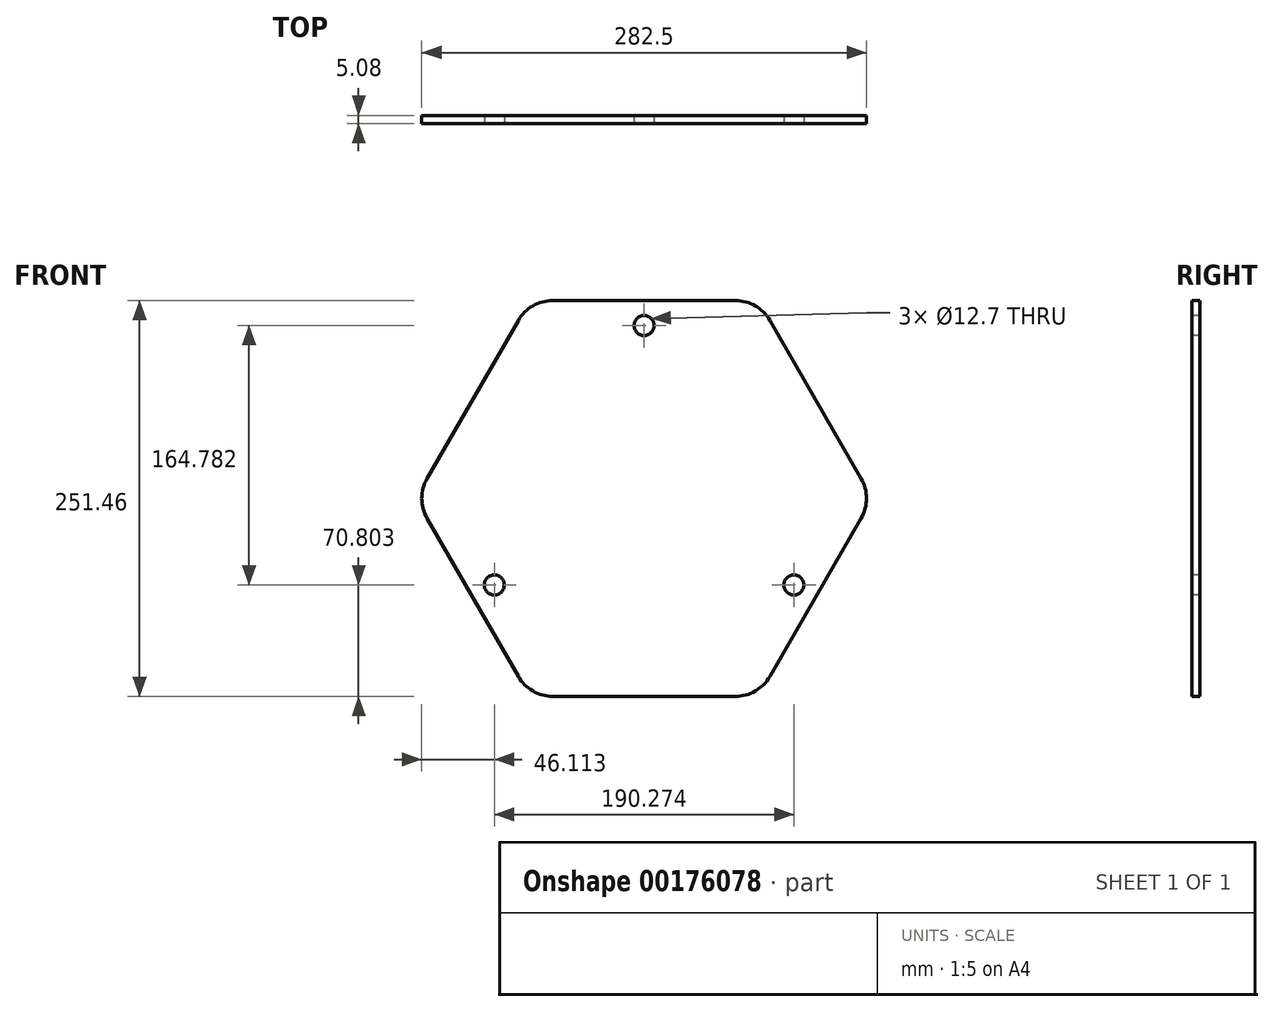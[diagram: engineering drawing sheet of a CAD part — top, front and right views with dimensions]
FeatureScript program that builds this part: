
annotation { "Feature Type Name" : "Feature", "Feature Type Description" : "" }
export const myFeature = defineFeature(function(context is Context, id is Id, definition is map)
    precondition{}
    {
        {
            var Q0;
            Q0=qCreatedBy(makeId("Front.planeOp"),FACE);
            var sketch = newSketch(context, id + "F0", { "sketchPlane" : qUnion([Q0])});
            skCircle(sketch, "E0.cCircle", {"center": v(0, 0) * mm, "radius": 125.73 * mm, "construction": true});
            skLineSegment(sketch, "E0.0", {"start": v(79.92, 113.03) * mm, "end": v(137.85, 12.7) * mm});
            skLineSegment(sketch, "E0.1", {"start": v(137.85, -12.7) * mm, "end": v(79.92, -113.03) * mm});
            skLineSegment(sketch, "E0.2", {"start": v(57.93, -125.73) * mm, "end": v(-57.93, -125.73) * mm});
            skLineSegment(sketch, "E0.3", {"start": v(-79.92, -113.03) * mm, "end": v(-137.85, -12.7) * mm});
            skLineSegment(sketch, "E0.4", {"start": v(-137.85, 12.7) * mm, "end": v(-79.92, 113.03) * mm});
            skLineSegment(sketch, "E0.5", {"start": v(-57.93, 125.73) * mm, "end": v(57.93, 125.73) * mm});
            skPoint(sketch, "E0.0.midPoint", {"position": v(108.89, 62.86) * mm});
            skPoint(sketch, "E1.0.midPoint", {"position": v(0, 93.98) * mm});
            skPoint(sketch, "E2.visualSharp", {"position": v(-72.6, 125.73) * mm});
            skArc(sketch, "E2.filletArc", {"start": v(-57.93, 125.73) * mm, "mid": v(-70.63, 122.33) * mm, "end": v(-79.92, 113.03) * mm});
            skPoint(sketch, "E3.visualSharp", {"position": v(72.6, 125.73) * mm});
            skArc(sketch, "E3.filletArc", {"start": v(79.92, 113.03) * mm, "mid": v(70.63, 122.33) * mm, "end": v(57.93, 125.73) * mm});
            skPoint(sketch, "E4.visualSharp", {"position": v(-145.18, 0) * mm});
            skArc(sketch, "E4.filletArc", {"start": v(-137.85, 12.7) * mm, "mid": v(-141.25, 0) * mm, "end": v(-137.85, -12.7) * mm});
            skPoint(sketch, "E5.visualSharp", {"position": v(145.18, 0) * mm});
            skArc(sketch, "E5.filletArc", {"start": v(137.85, -12.7) * mm, "mid": v(141.25, 0) * mm, "end": v(137.85, 12.7) * mm});
            skPoint(sketch, "E6.visualSharp", {"position": v(-72.6, -125.73) * mm});
            skArc(sketch, "E6.filletArc", {"start": v(-79.92, -113.03) * mm, "mid": v(-70.63, -122.33) * mm, "end": v(-57.93, -125.73) * mm});
            skPoint(sketch, "E7.visualSharp", {"position": v(72.6, -125.73) * mm});
            skArc(sketch, "E7.filletArc", {"start": v(57.93, -125.73) * mm, "mid": v(70.63, -122.33) * mm, "end": v(79.92, -113.03) * mm});
            skPoint(sketch, "E8.visualSharp", {"position": v(-54.26, 93.98) * mm});
            skPoint(sketch, "E9.visualSharp", {"position": v(54.26, 93.98) * mm});
            skPoint(sketch, "E10.visualSharp", {"position": v(108.52, 0) * mm});
            skPoint(sketch, "E11.visualSharp", {"position": v(54.26, -93.98) * mm});
            skPoint(sketch, "E12.visualSharp", {"position": v(-54.26, -93.98) * mm});
            skPoint(sketch, "E13.visualSharp", {"position": v(-108.52, 0) * mm});
            skSolve(sketch);
        }
        {
            var Q0;
            Q0=makeQuery(id+"F0.imprint","IMPRINT",FACE,{"disambiguationData":[TD([[makeQuery(id+"F0.imprint","IMPRINT",EDGE,{"derivedFrom":sQuery(id+"F0.wireOp",EDGE,"E0.0")}),-1.0]])]});
            extrude(context, id + "F1", {"entities" : qUnion([Q0]), "depth" : 5.08 * mm});
        }
        {
            var Q0;
            Q0=makeQuery(id+"F1.opExtrude","CAP_FACE",FACE,{"disambiguationData":[OSD([sQuery(id+"F0.wireOp",EDGE,"E0.0"),sQuery(id+"F0.wireOp",EDGE,"E0.1"),sQuery(id+"F0.wireOp",EDGE,"E0.2"),sQuery(id+"F0.wireOp",EDGE,"E0.3"),sQuery(id+"F0.wireOp",EDGE,"E0.4"),sQuery(id+"F0.wireOp",EDGE,"E0.5"),sQuery(id+"F0.wireOp",EDGE,"E1.0"),sQuery(id+"F0.wireOp",EDGE,"E1.1"),sQuery(id+"F0.wireOp",EDGE,"E1.2"),sQuery(id+"F0.wireOp",EDGE,"E1.3"),sQuery(id+"F0.wireOp",EDGE,"E1.4"),sQuery(id+"F0.wireOp",EDGE,"E1.5"),sQuery(id+"F0.wireOp",EDGE,"E2.filletArc"),sQuery(id+"F0.wireOp",EDGE,"E3.filletArc"),sQuery(id+"F0.wireOp",EDGE,"E4.filletArc"),sQuery(id+"F0.wireOp",EDGE,"E5.filletArc"),sQuery(id+"F0.wireOp",EDGE,"E6.filletArc"),sQuery(id+"F0.wireOp",EDGE,"E7.filletArc"),sQuery(id+"F0.wireOp",EDGE,"E8.filletArc"),sQuery(id+"F0.wireOp",EDGE,"E9.filletArc"),sQuery(id+"F0.wireOp",EDGE,"E10.filletArc"),sQuery(id+"F0.wireOp",EDGE,"E11.filletArc"),sQuery(id+"F0.wireOp",EDGE,"E12.filletArc"),sQuery(id+"F0.wireOp",EDGE,"E13.filletArc")])],"isStart":false});
            var sketch = newSketch(context, id + "F2", { "sketchPlane" : qUnion([Q0])});
            skLineSegment(sketch, "E14", {"start": v(0, 0) * mm, "end": v(0, 109.86) * mm, "construction": true});
            skPoint(sketch, "E15", {"position": v(70.63, 122.33) * mm});
            skCircle(sketch, "E16", {"center": v(0, 109.86) * mm, "radius": 6.35 * mm});
            skCircle(sketch, "E17.1.0", {"center": v(-95.14, -54.93) * mm, "radius": 6.35 * mm});
            skCircle(sketch, "E17.2.0", {"center": v(95.14, -54.93) * mm, "radius": 6.35 * mm});
            skPoint(sketch, "E17.center", {"position": v(0, 0) * mm});
            skSolve(sketch);
        }
        {
            var Q0;
            Q0=makeQuery(id+"F2.imprint","IMPRINT",FACE,{"disambiguationData":[TD([[makeQuery(id+"F2.imprint","IMPRINT",EDGE,{"derivedFrom":sQuery(id+"F2.wireOp",EDGE,"E16")}),1.0]])]});
            var Q1;
            Q1=makeQuery(id+"F2.imprint","IMPRINT",FACE,{"disambiguationData":[TD([[makeQuery(id+"F2.imprint","IMPRINT",EDGE,{"derivedFrom":sQuery(id+"F2.wireOp",EDGE,"E17.1.0")}),1.0]])]});
            var Q2;
            Q2=makeQuery(id+"F2.imprint","IMPRINT",FACE,{"disambiguationData":[TD([[makeQuery(id+"F2.imprint","IMPRINT",EDGE,{"derivedFrom":sQuery(id+"F2.wireOp",EDGE,"E17.2.0")}),1.0]])]});
            var Q3;
            Q3=makeQuery(id+"F2.imprint","IMPRINT",FACE,{"disambiguationData":[TD([[makeQuery(id+"F2.imprint","IMPRINT",EDGE,{"derivedFrom":sQuery(id+"F2.wireOp",EDGE,"E17.3.0")}),1.0]])]});
            var Q4;
            Q4=makeQuery(id+"F2.imprint","IMPRINT",FACE,{"disambiguationData":[TD([[makeQuery(id+"F2.imprint","IMPRINT",EDGE,{"derivedFrom":sQuery(id+"F2.wireOp",EDGE,"E17.4.0")}),1.0]])]});
            var Q5;
            Q5=makeQuery(id+"F2.imprint","IMPRINT",FACE,{"disambiguationData":[TD([[makeQuery(id+"F2.imprint","IMPRINT",EDGE,{"derivedFrom":sQuery(id+"F2.wireOp",EDGE,"E17.5.0")}),1.0]])]});
            extrude(context, id + "F3", {"entities" : qUnion([Q0, Q1, Q2, Q3, Q4, Q5]), "operationType" : NewBodyOperationType.REMOVE, "endBound" : BoundingType.THROUGH_ALL, "oppositeDirection" : true, "depth" : 25.4 * mm});
        }
    });
